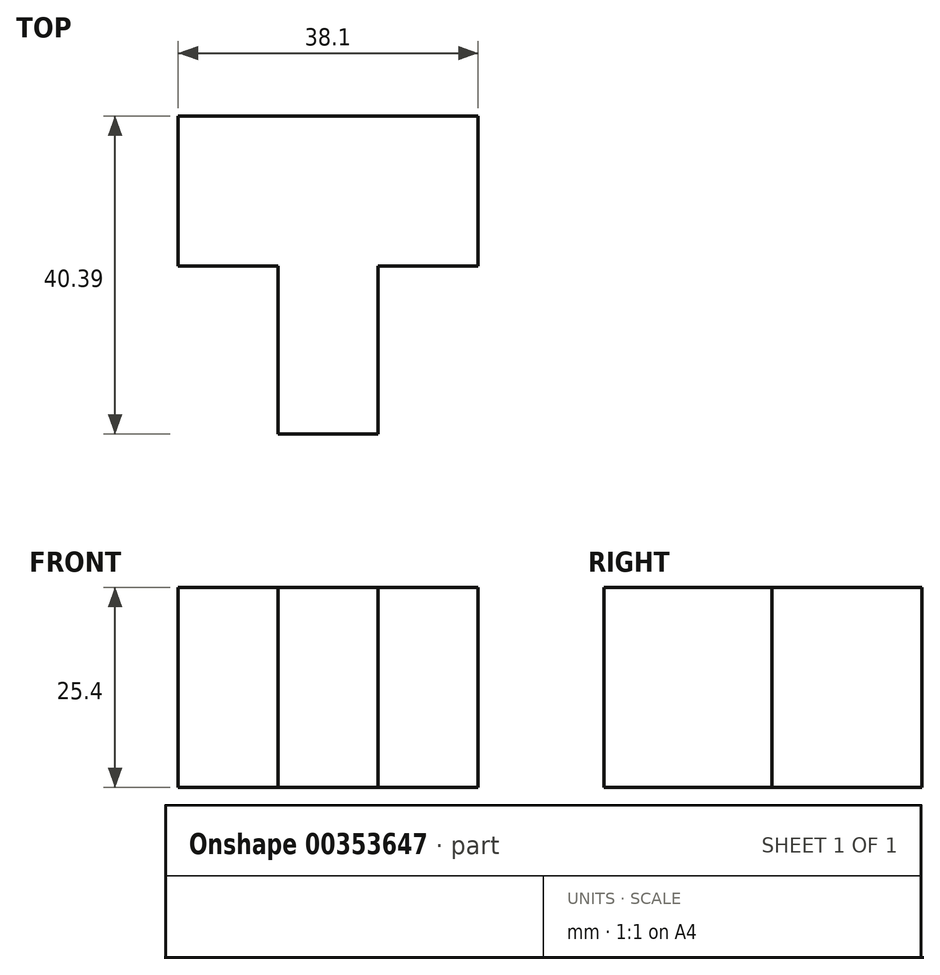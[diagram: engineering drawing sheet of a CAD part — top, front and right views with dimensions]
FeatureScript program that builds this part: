
annotation { "Feature Type Name" : "Feature", "Feature Type Description" : "" }
export const myFeature = defineFeature(function(context is Context, id is Id, definition is map)
    precondition{}
    {
        {
            var Q0;
            Q0=qCreatedBy(makeId("Top.planeOp"),FACE);
            var sketch = newSketch(context, id + "F0", { "sketchPlane" : qUnion([Q0])});
            skLineSegment(sketch, "E0", {"start": v(0, 40.4) * mm, "end": v(0, 21.34) * mm});
            skLineSegment(sketch, "E1", {"start": v(0, 21.34) * mm, "end": v(12.7, 21.34) * mm});
            skLineSegment(sketch, "E2", {"start": v(12.7, 21.34) * mm, "end": v(12.7, 0) * mm});
            skLineSegment(sketch, "E3", {"start": v(12.7, 0) * mm, "end": v(25.4, 0) * mm});
            skLineSegment(sketch, "E4", {"start": v(25.4, 0) * mm, "end": v(25.4, 21.34) * mm});
            skLineSegment(sketch, "E5", {"start": v(25.4, 21.34) * mm, "end": v(38.1, 21.34) * mm});
            skLineSegment(sketch, "E6", {"start": v(38.1, 21.34) * mm, "end": v(38.1, 40.4) * mm});
            skLineSegment(sketch, "E7", {"start": v(0, 40.4) * mm, "end": v(38.1, 40.4) * mm});
            skSolve(sketch);
        }
        {
            var Q0;
            Q0=makeQuery(id+"F0.imprint","IMPRINT",FACE,{"disambiguationData":[TD([[makeQuery(id+"F0.imprint","IMPRINT",EDGE,{"derivedFrom":sQuery(id+"F0.wireOp",EDGE,"E0")}),1.0]])]});
            extrude(context, id + "F1", {"entities" : qUnion([Q0]), "depth" : 25.4 * mm});
        }
    });
